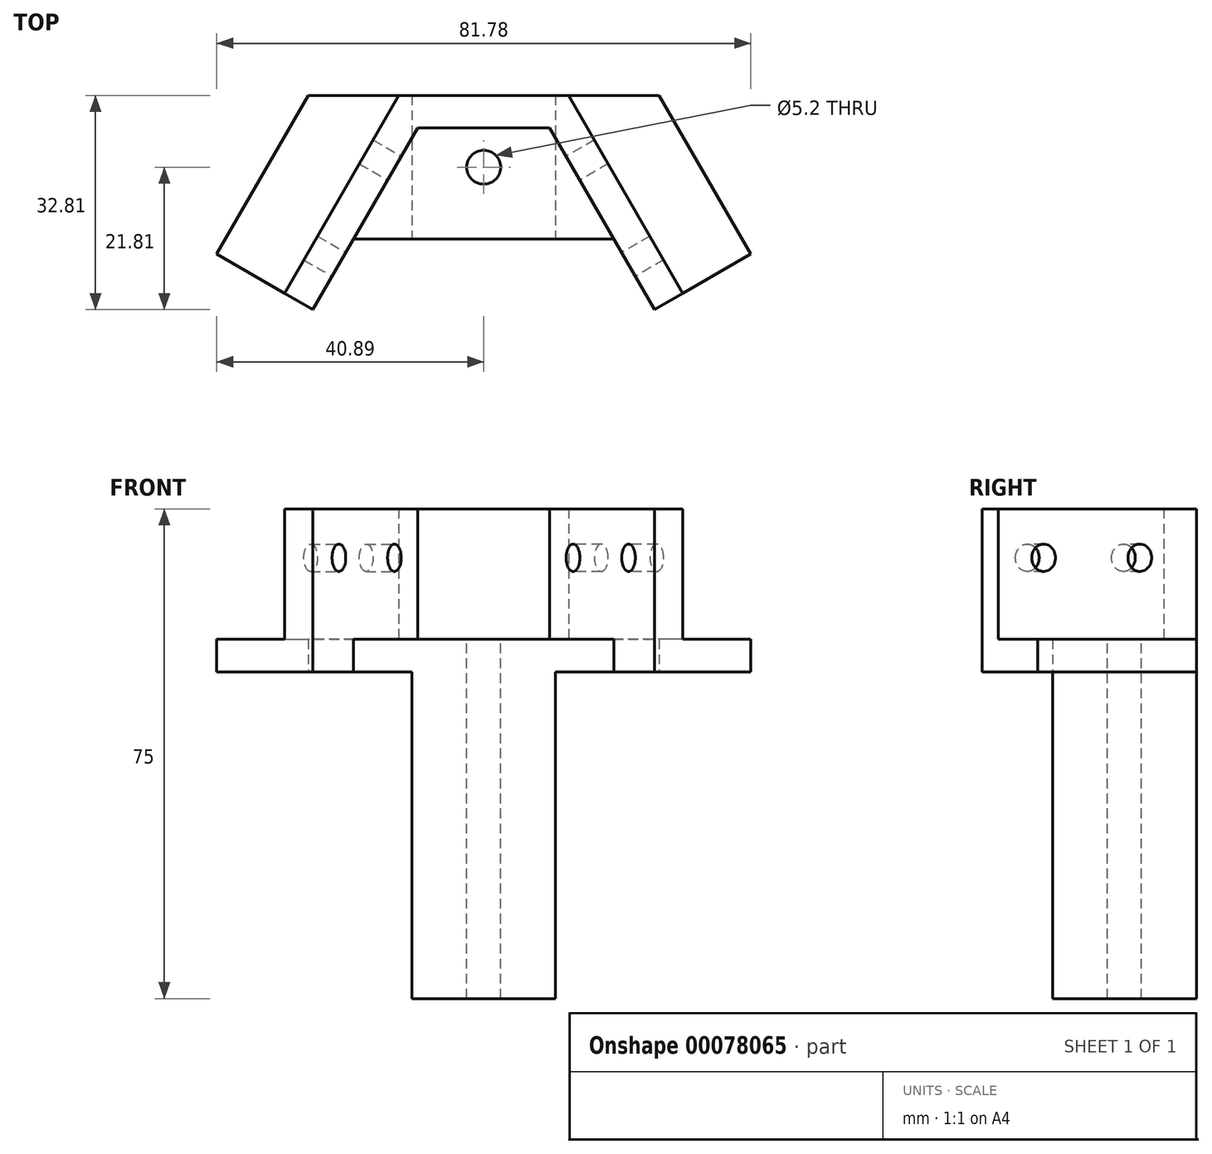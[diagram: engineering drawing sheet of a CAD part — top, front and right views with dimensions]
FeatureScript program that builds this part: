
annotation { "Feature Type Name" : "Feature", "Feature Type Description" : "" }
export const myFeature = defineFeature(function(context is Context, id is Id, definition is map)
    precondition{}
    {
        {
            var Q0;
            Q0=qCreatedBy(makeId("Top.planeOp"),FACE);
            var sketch = newSketch(context, id + "F0", { "sketchPlane" : qUnion([Q0])});
            skLineSegment(sketch, "E0", {"start": v(0, 0) * mm, "end": v(13, 0) * mm});
            skLineSegment(sketch, "E1", {"start": v(13, 0) * mm, "end": v(30.5, -30.31) * mm});
            skLineSegment(sketch, "E2", {"start": v(30.5, -30.31) * mm, "end": v(26.17, -32.81) * mm});
            skLineSegment(sketch, "E3", {"start": v(26.17, -32.81) * mm, "end": v(10.11, -5) * mm});
            skLineSegment(sketch, "E4", {"start": v(10.11, -5) * mm, "end": v(0, -5) * mm});
            skLineSegment(sketch, "E5", {"start": v(0, -5) * mm, "end": v(0, 0) * mm});
            skLineSegment(sketch, "E6", {"start": v(30.5, -30.31) * mm, "end": v(40.9, -24.31) * mm});
            skLineSegment(sketch, "E7", {"start": v(40.9, -24.31) * mm, "end": v(26.86, 0) * mm});
            skLineSegment(sketch, "E8", {"start": v(26.86, 0) * mm, "end": v(13, 0) * mm});
            skLineSegment(sketch, "E9", {"start": v(0, -5) * mm, "end": v(0, -22) * mm});
            skLineSegment(sketch, "E10", {"start": v(0, -22) * mm, "end": v(19.93, -22) * mm});
            skSolve(sketch);
        }
        {
            var Q0;
            {var subQ2=sQuery(id+"F0.wireOp",EDGE,"E4");Q0=makeQuery(id+"F0.imprint","IMPRINT",FACE,{"disambiguationData":[TD([[makeQuery(id+"F0.imprint","IMPRINT",EDGE,{"derivedFrom":subQ2}),1.0]])]});}
            var Q1;
            Q1=makeQuery(id+"F0.imprint","IMPRINT",FACE,{"disambiguationData":[TD([[makeQuery(id+"F0.imprint","IMPRINT",EDGE,{"derivedFrom":sQuery(id+"F0.wireOp",EDGE,"E0")}),-1.0]])]});
            var Q2;
            Q2=makeQuery(id+"F0.imprint","IMPRINT",FACE,{"disambiguationData":[TD([[makeQuery(id+"F0.imprint","IMPRINT",EDGE,{"derivedFrom":sQuery(id+"F0.wireOp",EDGE,"E1")}),1.0]])]});
            extrude(context, id + "F1", {"entities" : qUnion([Q0, Q1, Q2]), "depth" : 5 * mm, "offsetDistance" : 25 * mm});
        }
        {
            var Q0;
            Q0=makeQuery(id+"F0.imprint","IMPRINT",FACE,{"disambiguationData":[TD([[makeQuery(id+"F0.imprint","IMPRINT",EDGE,{"derivedFrom":sQuery(id+"F0.wireOp",EDGE,"E0")}),-1.0]])]});
            extrude(context, id + "F2", {"entities" : qUnion([Q0]), "operationType" : NewBodyOperationType.ADD, "depth" : 25 * mm, "offsetDistance" : 25 * mm});
        }
        {
            var Q0;
            Q0=makeQuery(id+"F2.opExtrude","SWEPT_FACE",FACE,{"disambiguationData":[OSD([sQuery(id+"F0.wireOp",EDGE,"E1")])]});
            var sketch = newSketch(context, id + "F3", { "sketchPlane" : qUnion([Q0])});
            skPoint(sketch, "E11", {"position": v(-33.5, 17.5) * mm});
            skPoint(sketch, "E12", {"position": v(-16.5, 17.5) * mm});
            skSolve(sketch);
        }
        {
            var Q0;
            Q0=sQuery(id+"F3.wireOp",VERTEX,"E11");
            var Q1;
            Q1=sQuery(id+"F3.wireOp",VERTEX,"E12");
            var Q2;
            Q2=makeQuery(id+"F1.opExtrude","SWEPT_BODY",BODY,{"disambiguationData":[OSD([sQuery(id+"F0.wireOp",EDGE,"E0"),sQuery(id+"F0.wireOp",EDGE,"E2"),sQuery(id+"F0.wireOp",EDGE,"E3"),sQuery(id+"F0.wireOp",EDGE,"E5"),sQuery(id+"F0.wireOp",EDGE,"E6"),sQuery(id+"F0.wireOp",EDGE,"E7"),sQuery(id+"F0.wireOp",EDGE,"E8"),sQuery(id+"F0.wireOp",EDGE,"E9"),sQuery(id+"F0.wireOp",EDGE,"E10")])]});
            hole(context, id + "F4", {"style" : HoleStyle.SIMPLE, "endStyle" : HoleEndStyle.THROUGH, "holeDiameter" : 4.2 * mm, "majorDiameter" : 5 * mm, "tappedDepth" : 12 * mm, "tapClearance" : 3, "locations" : qUnion([Q0, Q1]), "scope" : qUnion([Q2])});
        }
        {
            var Q0;
            Q0=makeQuery(id+"F1.opExtrude","SWEPT_BODY",BODY,{"disambiguationData":[OSD([sQuery(id+"F0.wireOp",EDGE,"E0"),sQuery(id+"F0.wireOp",EDGE,"E2"),sQuery(id+"F0.wireOp",EDGE,"E3"),sQuery(id+"F0.wireOp",EDGE,"E5"),sQuery(id+"F0.wireOp",EDGE,"E6"),sQuery(id+"F0.wireOp",EDGE,"E7"),sQuery(id+"F0.wireOp",EDGE,"E8"),sQuery(id+"F0.wireOp",EDGE,"E9"),sQuery(id+"F0.wireOp",EDGE,"E10")])]});
            var Q1;
            Q1=qCreatedBy(makeId("Right.planeOp"),FACE);
            mirror(context, id + "F5", {"operationType" : NewBodyOperationType.ADD, "entities" : qUnion([Q0]), "mirrorPlane" : qUnion([Q1])});
        }
        {
            var Q0;
            {var subQ0=makeQuery(id+"F1.opExtrude","CAP_FACE",FACE,{"disambiguationData":[OSD([sQuery(id+"F0.wireOp",EDGE,"E0"),sQuery(id+"F0.wireOp",EDGE,"E2"),sQuery(id+"F0.wireOp",EDGE,"E3"),sQuery(id+"F0.wireOp",EDGE,"E5"),sQuery(id+"F0.wireOp",EDGE,"E6"),sQuery(id+"F0.wireOp",EDGE,"E7"),sQuery(id+"F0.wireOp",EDGE,"E8"),sQuery(id+"F0.wireOp",EDGE,"E9"),sQuery(id+"F0.wireOp",EDGE,"E10")])],"isStart":true});Q0=makeQuery(id+"F5.boolean.opBoolean","MERGE",FACE,{"derivedFrom":[subQ0,makeQuery(id+"F5.opPattern","COPY",FACE,{"derivedFrom":subQ0,"instanceName":"1"})]});}
            var sketch = newSketch(context, id + "F6", { "sketchPlane" : qUnion([Q0])});
            skLineSegment(sketch, "E13.bottom", {"start": v(11, 0) * mm, "end": v(-11, 0) * mm});
            skLineSegment(sketch, "E13.top", {"start": v(11, 22) * mm, "end": v(-11, 22) * mm});
            skLineSegment(sketch, "E13.left", {"start": v(11, 0) * mm, "end": v(11, 22) * mm});
            skLineSegment(sketch, "E13.right", {"start": v(-11, 0) * mm, "end": v(-11, 22) * mm});
            skPoint(sketch, "E13.middle", {"position": v(0, 11) * mm});
            skSolve(sketch);
        }
        {
            var Q0;
            Q0 = qSketchRegion(id + "F6", true);
            extrude(context, id + "F7", {"entities" : qUnion([Q0]), "operationType" : NewBodyOperationType.ADD, "depth" : 50 * mm, "offsetDistance" : 25 * mm});
        }
        {
            var Q0;
            Q0=makeQuery(id+"F7.opExtrude","CAP_FACE",FACE,{"disambiguationData":[OSD([sQuery(id+"F6.wireOp",EDGE,"E13.bottom"),sQuery(id+"F6.wireOp",EDGE,"E13.top"),sQuery(id+"F6.wireOp",EDGE,"E13.left"),sQuery(id+"F6.wireOp",EDGE,"E13.right")])],"isStart":false});
            var sketch = newSketch(context, id + "F8", { "sketchPlane" : qUnion([Q0])});
            skPoint(sketch, "E14", {"position": v(0, 11) * mm});
            skSolve(sketch);
        }
        {
            var Q0;
            Q0=sQuery(id+"F8.wireOp",VERTEX,"E14");
            var Q1;
            Q1=makeQuery(id+"F1.opExtrude","SWEPT_BODY",BODY,{"disambiguationData":[OSD([sQuery(id+"F0.wireOp",EDGE,"E0"),sQuery(id+"F0.wireOp",EDGE,"E2"),sQuery(id+"F0.wireOp",EDGE,"E3"),sQuery(id+"F0.wireOp",EDGE,"E5"),sQuery(id+"F0.wireOp",EDGE,"E6"),sQuery(id+"F0.wireOp",EDGE,"E7"),sQuery(id+"F0.wireOp",EDGE,"E8"),sQuery(id+"F0.wireOp",EDGE,"E9"),sQuery(id+"F0.wireOp",EDGE,"E10")])]});
            hole(context, id + "F9", {"style" : HoleStyle.SIMPLE, "endStyle" : HoleEndStyle.THROUGH, "holeDiameter" : 5.2 * mm, "majorDiameter" : 5 * mm, "tappedDepth" : 12 * mm, "tapClearance" : 3, "locations" : qUnion([Q0]), "scope" : qUnion([Q1])});
        }
    });
